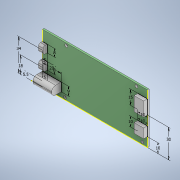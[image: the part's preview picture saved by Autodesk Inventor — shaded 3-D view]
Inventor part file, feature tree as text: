
AUTODESK INVENTOR PART (.ipt)
format: ipt  version: 2021 (Build 250183000, 183)  size: 182,272 bytes
history: native  units: mm
features: extrude x3, sketch x2, fillet x2, hole x1
ambient origin geometry x8: Origin, YZ Plane, XZ Plane, XY Plane, X Axis, Y Axis, Z Axis, Center Point
bodies: Solid1 (feature_tree)
feature tree (8):
  sketch  "Sketch1"  dims[d0=112.0mm d1=53.25mm d2=48.26mm d3=2.45mm d4=74.93mm d5=82.55mm d6=6.35mm d7=5.23mm d8=1.8mm d9=0.0mm]
  extrude  "Extrusion1"  Depth=1.8mm TaperAngle=0.0deg
  hole  "Hole1"  [1 undecoded]
  sketch  "Sketch2"  dims[d10=3.1mm d11=6.0mm d12=4.0mm d13=2.0mm d14=90.0deg d15=8.0mm d16=180.0deg d17=10.0mm d18=10.0mm d19=10.0mm d20=10.0mm d21=15.0mm d22=30.0mm d23=20.0mm d24=9.0mm d25=5.0mm d26=8.0mm d27=5.0mm d28=8.0mm d29=5.5mm d30=18.0mm d31=34.0mm d32=4.0mm d33=0.0mm d34=10.0mm d35=0.0mm d36=4.0mm d37=2.0mm d38=100.42mm d39=1.27mm]
  extrude  "Extrusion2"  Depth=10.0mm
  extrude  "Extrusion3"  Depth=10.0mm
  fillet  "Fillet1"  Radius=10.0mm
  fillet  "Fillet2"  Radius=15.0mm
note: 1 required parameter value undecoded (feature->parameter linkage not recoverable at this tier; creation-order binding heuristic only, values carry confidence <= 0.55)
